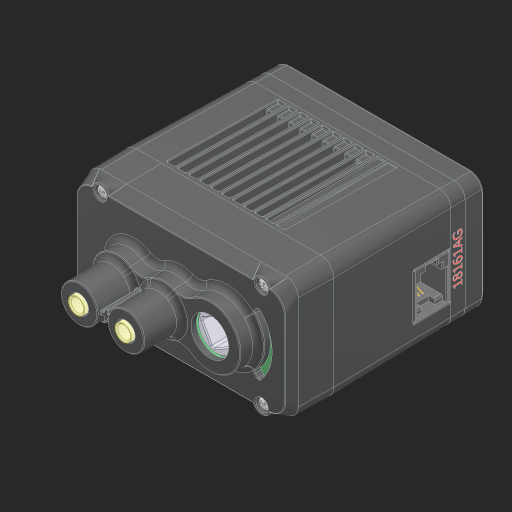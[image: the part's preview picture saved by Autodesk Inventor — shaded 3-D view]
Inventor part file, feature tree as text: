
AUTODESK INVENTOR PART (.ipt)
format: ipt  version: 2023 (Build 270158000, 158)  size: 8,709,120 bytes
history: native  units: in
note: dims shown in document units (in); Inventor stores cm internally (conversion verified against a paired STEP export)
features: other x15, extrude x2, sketch x2
ambient origin geometry x8: Origin, YZ Plane, XZ Plane, XY Plane, X Axis, Y Axis, Z Axis, Center Point
bodies: Solid1 (feature_tree), Solid2 (feature_tree), Solid4 (feature_tree), Solid6 (feature_tree), Solid7 (feature_tree), Solid8 (feature_tree), Solid9 (feature_tree), Solid14 (feature_tree), Solid16 (feature_tree), Solid17 (feature_tree), Solid18 (feature_tree), Solid19 (feature_tree), Solid20 (feature_tree), Solid21 (feature_tree), Solid22 (feature_tree)
feature tree (19):
  extrude  "Extrusion1"  TaperAngle=0.0deg  [1 undecoded]
  extrude  "Extrusion2"  Depth=0.1969in
  sketch  "Sketch1"  dims[d4=0.0in d5=0.0in]
  sketch  "Sketch2"  dims[d48=0.0197in d73=0.1969in d74=0.0148in d75=0.0591in d121=0.0984in d126=0.0394in d131=0.002in d132=0.0in d133=0.002in d134=0.0in]
  other  "276-4840-001 Rev38_1:1"
  other  "276-4840-005 Rev27_2:1"
  other  "276-4840-902 Rev2_24:1"
  other  "276-4840-004 Rev16_4:1"
  other  "276-4840-015 Rev7_5:1"
  other  "276-4840-015 Rev7_6:1"
  other  "276-4840-015 Rev7_7:1"
  other  "276-4840-003 Rev27_12:1"
  other  "276-4840-018 Rev6_18:1"
  other  "276-4840-059 Rev2_19:1"
  other  "276-4840-062 Rev1_20:1"
  other  "276-4840-062 Rev1_21:1"
  other  "276-4840-062 Rev1_22:1"
  other  "276-4840-043 Rev8_14:1"
  other  "276-4840-043 Rev8_15:1"
note: 1 required parameter value undecoded (feature->parameter linkage not recoverable at this tier; creation-order binding heuristic only, values carry confidence <= 0.55)
